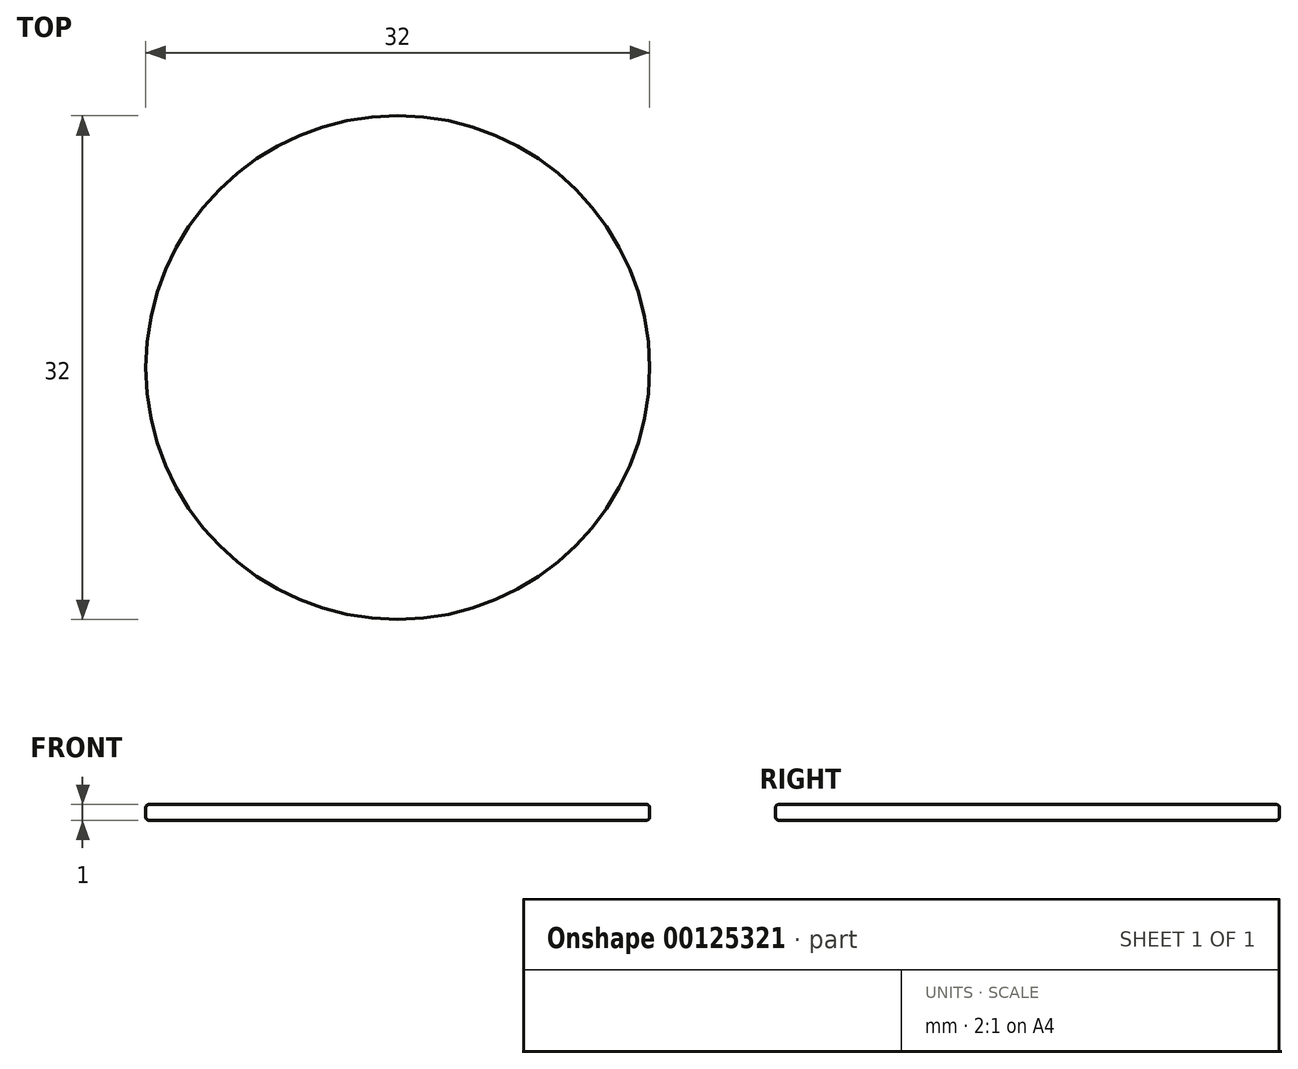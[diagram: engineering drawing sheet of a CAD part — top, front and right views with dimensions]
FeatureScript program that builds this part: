
annotation { "Feature Type Name" : "Feature", "Feature Type Description" : "" }
export const myFeature = defineFeature(function(context is Context, id is Id, definition is map)
    precondition{}
    {
        {
            var Q0;
            Q0=qCreatedBy(makeId("Top.planeOp"),FACE);
            var sketch = newSketch(context, id + "F0", { "sketchPlane" : qUnion([Q0])});
            skCircle(sketch, "E0", {"center": v(0, 0) * mm, "radius": 16 * mm});
            skSolve(sketch);
        }
        {
            var Q0;
            Q0 = qSketchRegion(id + "F0", true);
            extrude(context, id + "F1", {"entities" : qUnion([Q0]), "depth" : 1 * mm});
        }
        {
            var Q0;
            Q0=makeQuery(id+"F1.opExtrude","SWEPT_FACE",FACE,{"disambiguationData":[OSD([sQuery(id+"F0.wireOp",EDGE,"E0")])]});
            fillet(context, id + "F2", {"entities" : qUnion([Q0]), "radius" : .2 * mm, "tangentPropagation" : true, "allowEdgeOverflow" : false});
        }
    });
